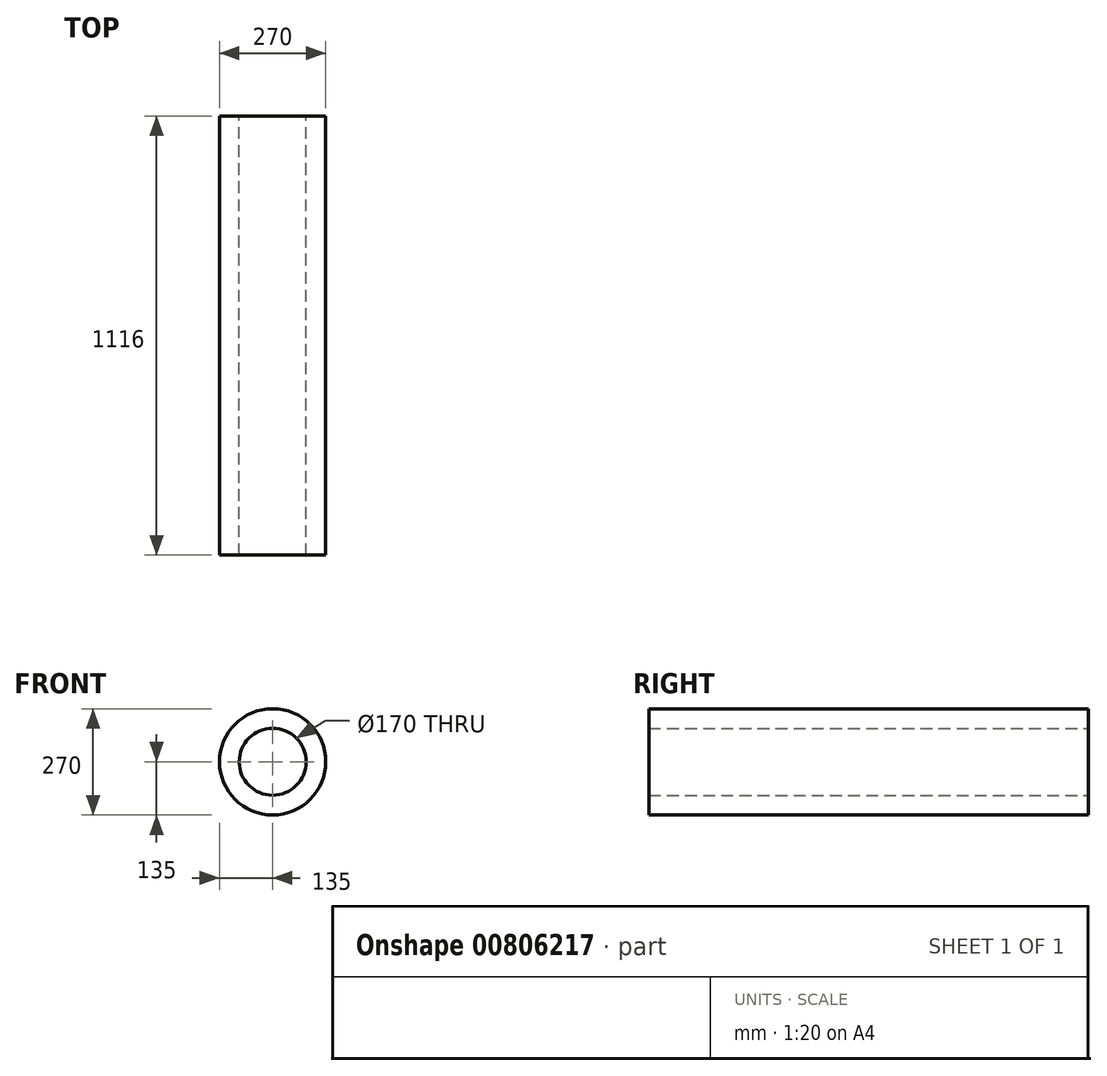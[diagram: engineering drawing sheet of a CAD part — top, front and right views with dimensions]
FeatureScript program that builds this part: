
annotation { "Feature Type Name" : "Feature", "Feature Type Description" : "" }
export const myFeature = defineFeature(function(context is Context, id is Id, definition is map)
    precondition{}
    {
        {
            var Q0;
            Q0=qCreatedBy(makeId("Front.planeOp"),FACE);
            var sketch = newSketch(context, id + "F0", { "sketchPlane" : qUnion([Q0])});
            skCircle(sketch, "E0", {"center": v(0, 0) * mm, "radius": 85 * mm});
            skCircle(sketch, "E1", {"center": v(0, 0) * mm, "radius": 135 * mm});
            skSolve(sketch);
        }
        {
            var Q0;
            Q0=qSketchRegion(id+"F0",true);
            extrude(context, id + "F1", {"entities" : qUnion([Q0]), "depth" : 1116 * mm, "offsetDistance" : 25 * mm});
        }
    });
